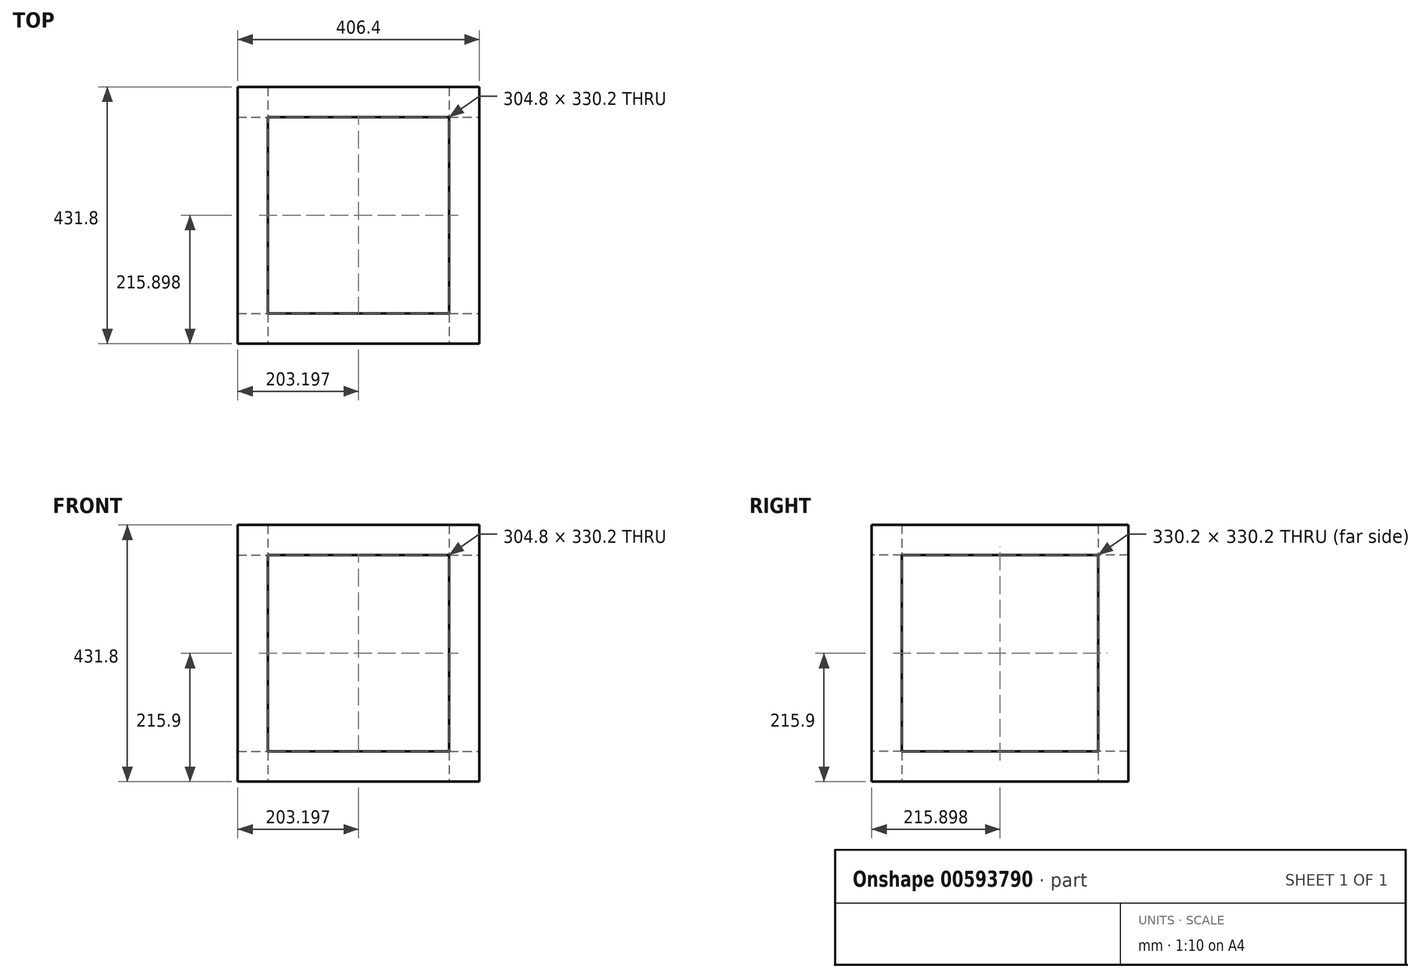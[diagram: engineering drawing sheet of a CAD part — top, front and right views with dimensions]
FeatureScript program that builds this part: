
annotation { "Feature Type Name" : "Feature", "Feature Type Description" : "" }
export const myFeature = defineFeature(function(context is Context, id is Id, definition is map)
    precondition{}
    {
        {
            var Q0;
            Q0=qCreatedBy(makeId("Top.planeOp"),FACE);
            var sketch = newSketch(context, id + "F0", { "sketchPlane" : qUnion([Q0])});
            skLineSegment(sketch, "E0.bottom", {"start": v(-60.6, 45.1) * mm, "end": v(345.8, 45.1) * mm});
            skLineSegment(sketch, "E0.top", {"start": v(-60.6, -386.7) * mm, "end": v(345.8, -386.7) * mm});
            skLineSegment(sketch, "E0.left", {"start": v(-60.6, 45.1) * mm, "end": v(-60.6, -386.7) * mm});
            skLineSegment(sketch, "E0.right", {"start": v(345.8, 45.1) * mm, "end": v(345.8, -386.7) * mm});
            skSolve(sketch);
        }
        {
            var Q0;
            Q0=makeQuery(id+"F0.imprint","IMPRINT",FACE,{"disambiguationData":[TD([[makeQuery(id+"F0.imprint","IMPRINT",EDGE,{"derivedFrom":sQuery(id+"F0.wireOp",EDGE,"E0.bottom")}),-1.0]])]});
            extrude(context, id + "F1", {"entities" : qUnion([Q0]), "depth" : 431.8 * mm, "offsetDistance" : 25.4 * mm});
        }
        {
            var Q0;
            Q0=makeQuery(id+"F1.opExtrude","SWEPT_FACE",FACE,{"disambiguationData":[OSD([sQuery(id+"F0.wireOp",EDGE,"E0.top")])]});
            var sketch = newSketch(context, id + "F2", { "sketchPlane" : qUnion([Q0])});
            skLineSegment(sketch, "E1.bottom", {"start": v(-9.8, 381) * mm, "end": v(295, 381) * mm});
            skLineSegment(sketch, "E1.top", {"start": v(-9.8, 50.8) * mm, "end": v(295, 50.8) * mm});
            skLineSegment(sketch, "E1.left", {"start": v(-9.8, 381) * mm, "end": v(-9.8, 50.8) * mm});
            skLineSegment(sketch, "E1.right", {"start": v(295, 381) * mm, "end": v(295, 50.8) * mm});
            skSolve(sketch);
        }
        {
            var Q0;
            Q0=makeQuery(id+"F2.imprint","IMPRINT",FACE,{"disambiguationData":[TD([[makeQuery(id+"F2.imprint","IMPRINT",EDGE,{"derivedFrom":sQuery(id+"F2.wireOp",EDGE,"E1.bottom")}),-1.0]])]});
            extrude(context, id + "F3", {"entities" : qUnion([Q0]), "operationType" : NewBodyOperationType.REMOVE, "oppositeDirection" : true, "depth" : 1270 * mm, "offsetDistance" : 25.4 * mm});
        }
        {
            var Q0;
            Q0=makeQuery(id+"F1.opExtrude","CAP_FACE",FACE,{"disambiguationData":[OSD([sQuery(id+"F0.wireOp",EDGE,"E0.bottom"),sQuery(id+"F0.wireOp",EDGE,"E0.top"),sQuery(id+"F0.wireOp",EDGE,"E0.left"),sQuery(id+"F0.wireOp",EDGE,"E0.right")])],"isStart":true});
            var sketch = newSketch(context, id + "F4", { "sketchPlane" : qUnion([Q0])});
            skLineSegment(sketch, "E2.bottom", {"start": v(-9.8, 335.9) * mm, "end": v(295, 335.9) * mm});
            skLineSegment(sketch, "E2.top", {"start": v(-9.8, 5.7) * mm, "end": v(295, 5.7) * mm});
            skLineSegment(sketch, "E2.left", {"start": v(-9.8, 335.9) * mm, "end": v(-9.8, 5.7) * mm});
            skLineSegment(sketch, "E2.right", {"start": v(295, 335.9) * mm, "end": v(295, 5.7) * mm});
            skSolve(sketch);
        }
        {
            var Q0;
            Q0=makeQuery(id+"F4.imprint","IMPRINT",FACE,{"disambiguationData":[TD([[makeQuery(id+"F4.imprint","IMPRINT",EDGE,{"derivedFrom":sQuery(id+"F4.wireOp",EDGE,"E2.bottom")}),-1.0]])]});
            extrude(context, id + "F5", {"entities" : qUnion([Q0]), "operationType" : NewBodyOperationType.REMOVE, "oppositeDirection" : true, "depth" : 754.38 * mm, "offsetDistance" : 25.4 * mm});
        }
        {
            var Q0;
            Q0=makeQuery(id+"F1.opExtrude","SWEPT_FACE",FACE,{"disambiguationData":[OSD([sQuery(id+"F0.wireOp",EDGE,"E0.right")])]});
            var sketch = newSketch(context, id + "F6", { "sketchPlane" : qUnion([Q0])});
            skLineSegment(sketch, "E3.bottom", {"start": v(-335.9, 381) * mm, "end": v(-5.7, 381) * mm});
            skLineSegment(sketch, "E3.top", {"start": v(-335.9, 50.8) * mm, "end": v(-5.7, 50.8) * mm});
            skLineSegment(sketch, "E3.left", {"start": v(-335.9, 381) * mm, "end": v(-335.9, 50.8) * mm});
            skLineSegment(sketch, "E3.right", {"start": v(-5.7, 381) * mm, "end": v(-5.7, 50.8) * mm});
            skSolve(sketch);
        }
        {
            var Q0;
            Q0=makeQuery(id+"F6.imprint","IMPRINT",FACE,{"disambiguationData":[TD([[makeQuery(id+"F6.imprint","IMPRINT",EDGE,{"derivedFrom":sQuery(id+"F6.wireOp",EDGE,"E3.bottom")}),-1.0]])]});
            extrude(context, id + "F7", {"entities" : qUnion([Q0]), "operationType" : NewBodyOperationType.REMOVE, "oppositeDirection" : true, "depth" : 1270 * mm, "offsetDistance" : 25.4 * mm});
        }
    });
